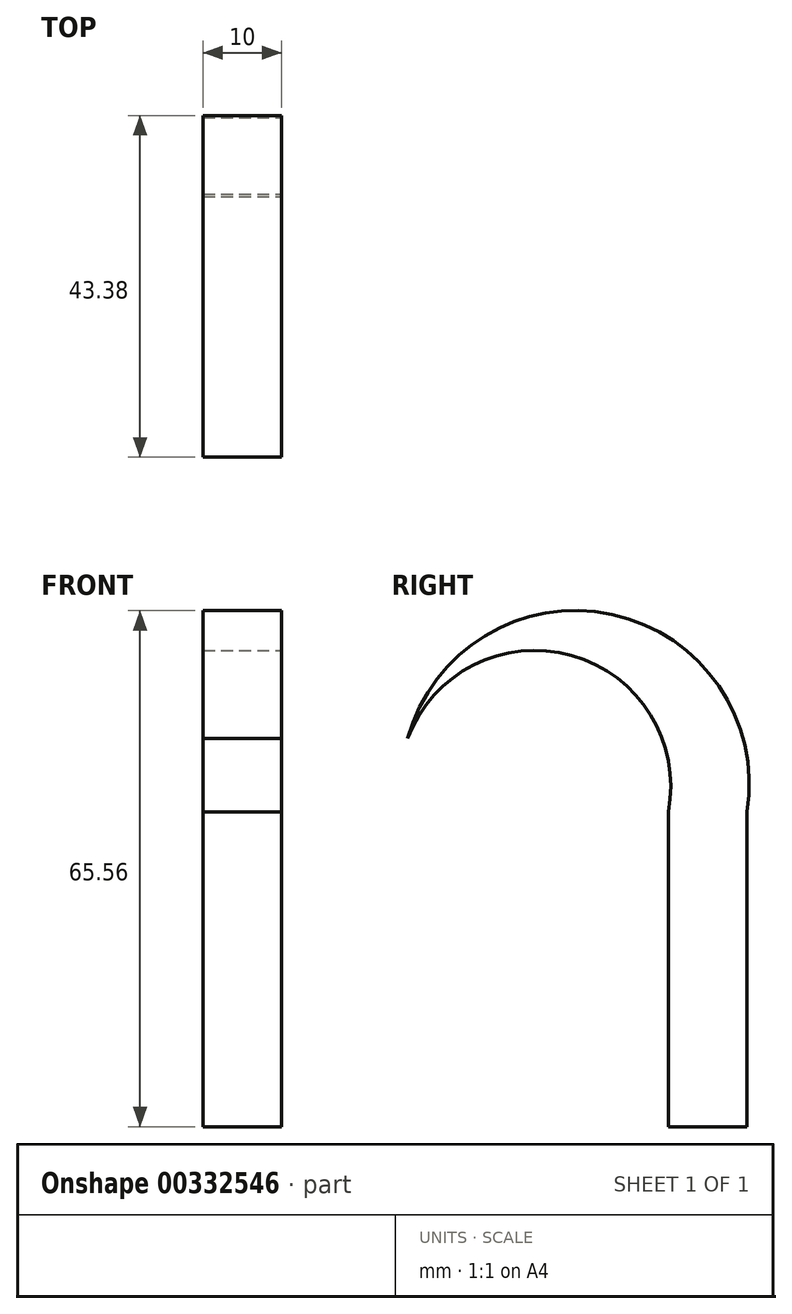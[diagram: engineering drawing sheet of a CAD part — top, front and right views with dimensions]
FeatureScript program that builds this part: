
annotation { "Feature Type Name" : "Feature", "Feature Type Description" : "" }
export const myFeature = defineFeature(function(context is Context, id is Id, definition is map)
    precondition{}
    {
        {
            var Q0;
            Q0=qCreatedBy(makeId("Top.planeOp"),FACE);
            var sketch = newSketch(context, id + "F0", { "sketchPlane" : qUnion([Q0])});
            skLineSegment(sketch, "E0.bottom", {"start": v(-8.8, 6.55) * mm, "end": v(11.2, 6.55) * mm});
            skLineSegment(sketch, "E0.top", {"start": v(-8.8, -3.45) * mm, "end": v(11.2, -3.45) * mm});
            skLineSegment(sketch, "E0.left", {"start": v(-8.8, 6.55) * mm, "end": v(-8.8, -3.45) * mm});
            skLineSegment(sketch, "E0.right", {"start": v(11.2, 6.55) * mm, "end": v(11.2, -3.45) * mm});
            skSolve(sketch);
        }
        {
            var Q0;
            Q0=makeQuery(id+"F0.imprint","IMPRINT",FACE,{"disambiguationData":[TD([[makeQuery(id+"F0.imprint","IMPRINT",EDGE,{"derivedFrom":sQuery(id+"F0.wireOp",EDGE,"E0.bottom")}),-1.0]])]});
            extrude(context, id + "F1", {"entities" : qUnion([Q0]), "depth" : 40 * mm});
        }
        {
            var Q0;
            Q0=makeQuery(id+"F1.opExtrude","SWEPT_FACE",FACE,{"disambiguationData":[OSD([sQuery(id+"F0.wireOp",EDGE,"E0.right")])]});
            var sketch = newSketch(context, id + "F2", { "sketchPlane" : qUnion([Q0])});
            skArc(sketch, "E1", {"start": v(-3.45, 40) * mm, "mid": v(-15.74, 59.86) * mm, "end": v(-36.56, 49.29) * mm});
            skArc(sketch, "E2", {"start": v(6.55, 40) * mm, "mid": v(-10.6, 65.07) * mm, "end": v(-36.56, 49.29) * mm});
            skSolve(sketch);
        }
        {
            var Q0;
            Q0=makeQuery(id+"F2.imprint","IMPRINT",FACE,{"disambiguationData":[TD([[makeQuery(id+"F2.imprint","IMPRINT",EDGE,{"derivedFrom":sQuery(id+"F2.wireOp",EDGE,"E1")}),-1.0]])]});
            extrude(context, id + "F3", {"entities" : qUnion([Q0]), "operationType" : NewBodyOperationType.ADD, "oppositeDirection" : true, "depth" : 20 * mm});
        }
        {
            var Q0;
            Q0=makeQuery(id+"F1.opExtrude","SWEPT_FACE",FACE,{"disambiguationData":[OSD([sQuery(id+"F0.wireOp",EDGE,"E0.top")])]});
            var sketch = newSketch(context, id + "F4", { "sketchPlane" : qUnion([Q0])});
            skLineSegment(sketch, "E3", {"start": v(1.2, 0) * mm, "end": v(11.2, 0) * mm});
            skLineSegment(sketch, "E4", {"start": v(11.2, 0) * mm, "end": v(6.2, 0) * mm});
            skLineSegment(sketch, "E5", {"start": v(6.2, 0) * mm, "end": v(11.2, 20) * mm});
            skLineSegment(sketch, "E6", {"start": v(11.2, 20) * mm, "end": v(-8.8, 20) * mm});
            skLineSegment(sketch, "E7", {"start": v(-8.8, 20) * mm, "end": v(-8.8, 0) * mm});
            skLineSegment(sketch, "E8", {"start": v(-8.8, 0) * mm, "end": v(1.2, 0) * mm});
            skLineSegment(sketch, "E9", {"start": v(-3.8, 0) * mm, "end": v(-8.8, 20) * mm});
            skSolve(sketch);
        }
        {
            var Q0;
            {var subQ0=sQuery(id+"F4.wireOp",EDGE,"E4");Q0=makeQuery(id+"F4.imprint","IMPRINT",FACE,{"disambiguationData":[TD([[makeQuery(id+"F4.imprint","IMPRINT",EDGE,{"derivedFrom":subQ0}),1.0]])]});}
            var Q1;
            {var subQ0=sQuery(id+"F4.wireOp",EDGE,"E7");Q1=makeQuery(id+"F4.imprint","IMPRINT",FACE,{"disambiguationData":[TD([[makeQuery(id+"F4.imprint","IMPRINT",EDGE,{"derivedFrom":subQ0}),1.0]])]});}
            extrude(context, id + "F5", {"entities" : qUnion([Q0, Q1]), "operationType" : NewBodyOperationType.REMOVE, "oppositeDirection" : true, "depth" : 25 * mm});
        }
        {
            var Q0;
            Q0=makeQuery(id+"F1.opExtrude","SWEPT_FACE",FACE,{"disambiguationData":[OSD([sQuery(id+"F0.wireOp",EDGE,"E0.bottom")])]});
            var sketch = newSketch(context, id + "F6", { "sketchPlane" : qUnion([Q0])});
            skLineSegment(sketch, "E10", {"start": v(3.8, 0) * mm, "end": v(3.8, 66.68) * mm});
            skLineSegment(sketch, "E11", {"start": v(3.8, 66.68) * mm, "end": v(-6.2, 66.68) * mm});
            skLineSegment(sketch, "E12", {"start": v(-6.2, 66.68) * mm, "end": v(-6.2, 0) * mm});
            skSolve(sketch);
        }
        {
            var Q0;
            Q0 = qSketchRegion(id + "F6", true);
            var Q1;
            {var subQ1=sQuery(id+"F0.wireOp",EDGE,"E0.bottom");var subQ5=makeQuery(id+"F1.opExtrude","SWEPT_EDGE",EDGE,{"disambiguationData":[OSD([subQ1,sQuery(id+"F0.wireOp",EDGE,"E0.left")])]});Q1=makeQuery(id+"F6.imprint","IMPRINT",FACE,{"disambiguationData":[TD([[makeQuery(id+"F6.imprint","IMPRINT",EDGE,{"derivedFrom":subQ5}),-1.0]])]});}
            var Q2;
            {var subQ1=sQuery(id+"F0.wireOp",EDGE,"E0.bottom");var subQ3=sQuery(id+"F0.wireOp",EDGE,"E0.right");var subQ6=makeQuery(id+"F1.opExtrude","SWEPT_EDGE",EDGE,{"disambiguationData":[OSD([subQ1,subQ3])]});Q2=makeQuery(id+"F6.imprint","IMPRINT",FACE,{"disambiguationData":[TD([[makeQuery(id+"F6.imprint","IMPRINT",EDGE,{"derivedFrom":subQ6}),1.0]])]});}
            extrude(context, id + "F7", {"entities" : qUnion([Q0, Q1, Q2]), "operationType" : NewBodyOperationType.REMOVE, "oppositeDirection" : true, "depth" : 25 * mm});
        }
        {
            var Q0;
            Q0=makeQuery(id+"F2.imprint","IMPRINT",FACE,{"disambiguationData":[TD([[makeQuery(id+"F2.imprint","IMPRINT",EDGE,{"derivedFrom":sQuery(id+"F2.wireOp",EDGE,"E1")}),-1.0]])]});
            extrude(context, id + "F8", {"entities" : qUnion([Q0]), "operationType" : NewBodyOperationType.ADD, "oppositeDirection" : true, "depth" : 15 * mm});
        }
        {
            var Q0;
            Q0=makeQuery(id+"F8.opExtrude","CAP_FACE",FACE,{"disambiguationData":[OSD([sQuery(id+"F0.wireOp",EDGE,"E0.right"),sQuery(id+"F2.wireOp",EDGE,"E1"),sQuery(id+"F2.wireOp",EDGE,"E2")])],"isStart":true});
            var Q1;
            {var subQ0=sQuery(id+"F0.wireOp",EDGE,"E0.right");Q1=makeQuery(id+"F3.boolean.opBoolean","MERGE",FACE,{"derivedFrom":[makeQuery(id+"F1.opExtrude","SWEPT_FACE",FACE,{"disambiguationData":[OSD([subQ0])]}),makeQuery(id+"F3.opExtrude","CAP_FACE",FACE,{"disambiguationData":[OSD([subQ0,sQuery(id+"F2.wireOp",EDGE,"E1"),sQuery(id+"F2.wireOp",EDGE,"E2")])],"isStart":true})]});}
            extrude(context, id + "F9", {"entities" : qUnion([Q0, Q1]), "operationType" : NewBodyOperationType.REMOVE, "oppositeDirection" : true, "depth" : 5 * mm});
        }
        {
            var Q0;
            Q0=makeQuery(id+"F3.boolean.opBoolean","MERGE",FACE,{"derivedFrom":[makeQuery(id+"F1.opExtrude","SWEPT_FACE",FACE,{"disambiguationData":[OSD([sQuery(id+"F0.wireOp",EDGE,"E0.left")])]}),makeQuery(id+"F3.opExtrude","CAP_FACE",FACE,{"disambiguationData":[OSD([sQuery(id+"F0.wireOp",EDGE,"E0.right"),sQuery(id+"F2.wireOp",EDGE,"E1"),sQuery(id+"F2.wireOp",EDGE,"E2")])],"isStart":false})]});
            extrude(context, id + "F10", {"entities" : qUnion([Q0]), "operationType" : NewBodyOperationType.REMOVE, "oppositeDirection" : true, "depth" : 5 * mm});
        }
    });
